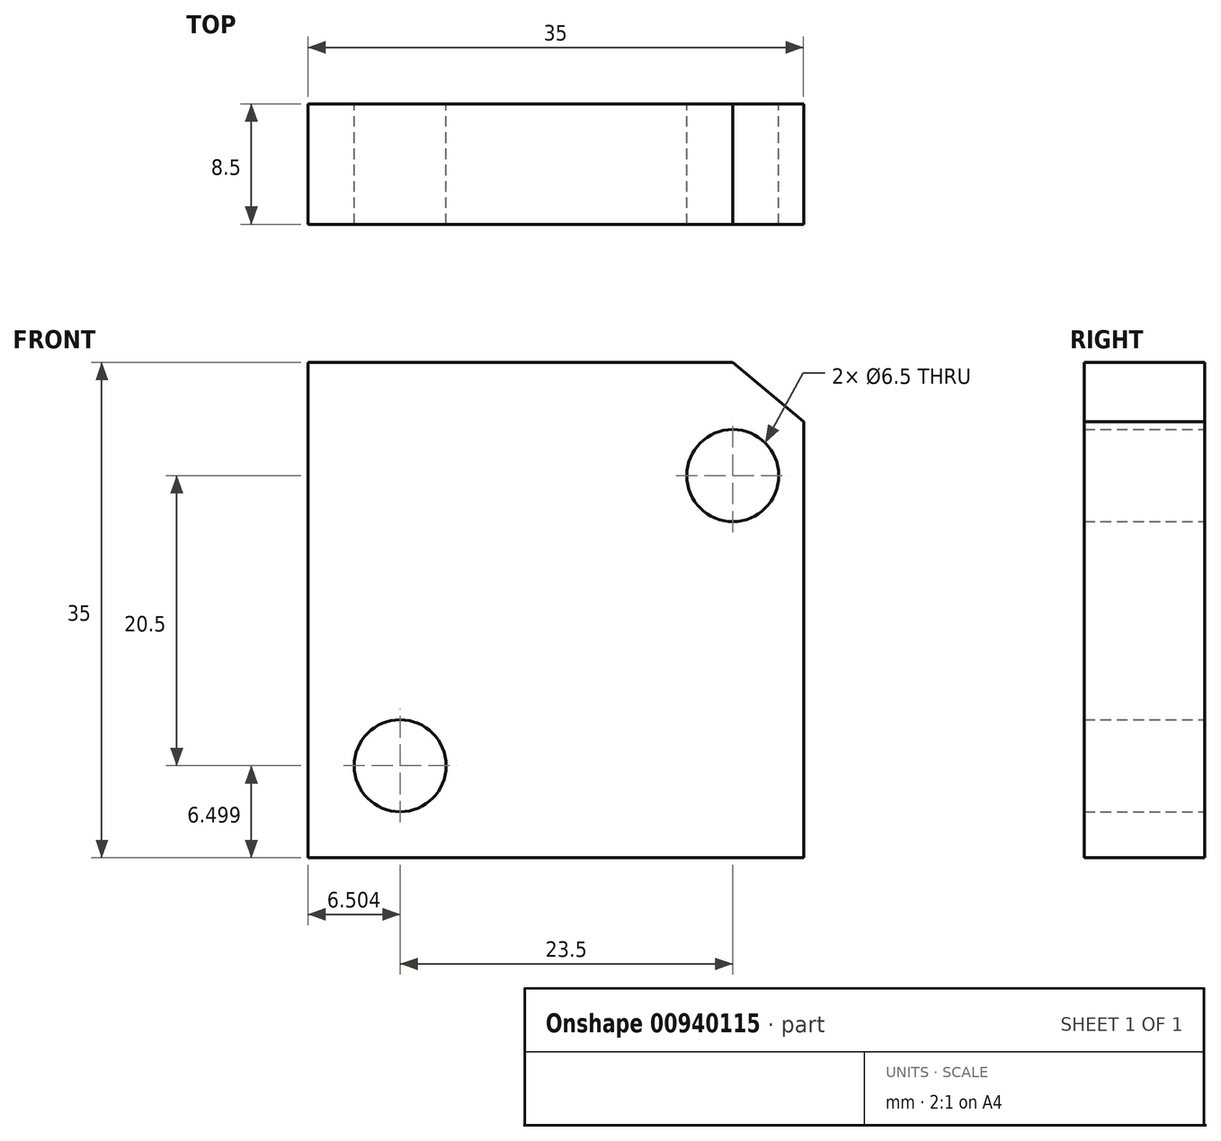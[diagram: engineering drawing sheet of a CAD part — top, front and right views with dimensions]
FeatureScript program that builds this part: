
annotation { "Feature Type Name" : "Feature", "Feature Type Description" : "" }
export const myFeature = defineFeature(function(context is Context, id is Id, definition is map)
    precondition{}
    {
        {
            var Q0;
            Q0=qCreatedBy(makeId("Front.planeOp"),FACE);
            var sketch = newSketch(context, id + "F0", { "sketchPlane" : qUnion([Q0])});
            skLineSegment(sketch, "E0.top", {"start": v(-61.22, -16.41) * mm, "end": v(-26.22, -16.41) * mm});
            skLineSegment(sketch, "E0.right", {"start": v(-26.22, 14.4) * mm, "end": v(-26.22, -16.41) * mm});
            skCircle(sketch, "E1", {"center": v(-31.22, 10.59) * mm, "radius": 3.25 * mm});
            skLineSegment(sketch, "E2", {"start": v(-61.22, 18.59) * mm, "end": v(-31.22, 18.59) * mm});
            skCircle(sketch, "E3", {"center": v(-54.72, -9.91) * mm, "radius": 3.25 * mm});
            skLineSegment(sketch, "E4", {"start": v(-61.22, -16.41) * mm, "end": v(-61.22, 18.59) * mm});
            skLineSegment(sketch, "E5", {"start": v(-31.22, 18.59) * mm, "end": v(-26.22, 14.4) * mm});
            skSolve(sketch);
        }
        {
            var Q0;
            Q0=makeQuery(id+"F0.imprint","IMPRINT",FACE,{"disambiguationData":[TD([[makeQuery(id+"F0.imprint","IMPRINT",EDGE,{"derivedFrom":sQuery(id+"F0.wireOp",EDGE,"E0.top")}),1.0]])]});
            extrude(context, id + "F1", {"entities" : qUnion([Q0]), "depth" : 8.5 * mm, "offsetDistance" : 25 * mm});
        }
    });
